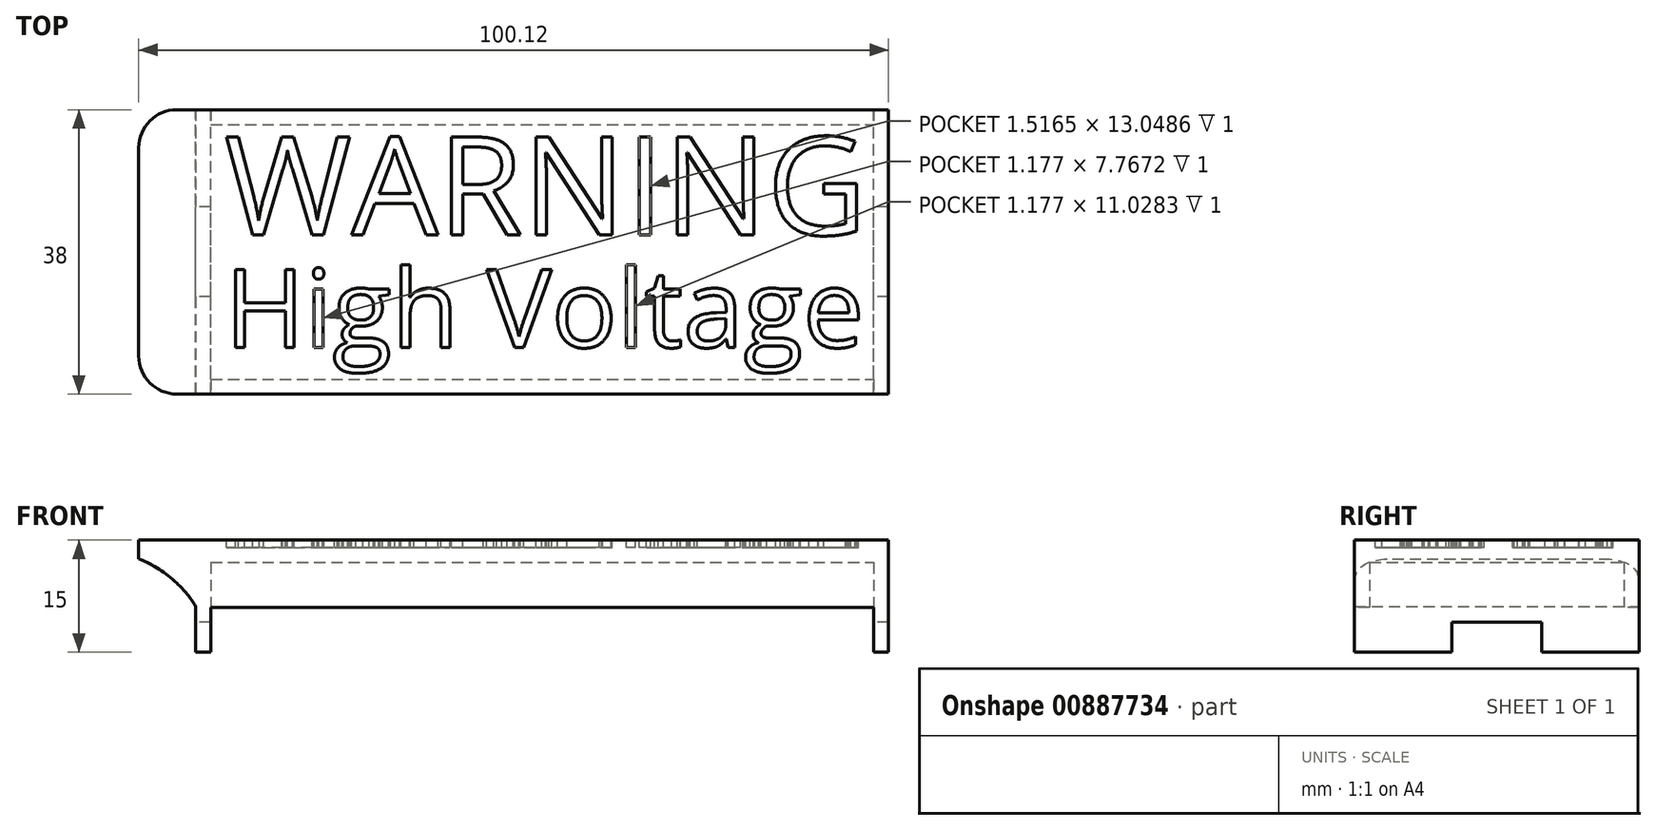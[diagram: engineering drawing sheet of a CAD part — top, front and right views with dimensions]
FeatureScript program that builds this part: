
annotation { "Feature Type Name" : "Feature", "Feature Type Description" : "" }
export const myFeature = defineFeature(function(context is Context, id is Id, definition is map)
    precondition{}
    {
        {
            var Q0;
            Q0=qCreatedBy(makeId("Top.planeOp"),FACE);
            var sketch = newSketch(context, id + "F0", { "sketchPlane" : qUnion([Q0])});
            skLineSegment(sketch, "E0.bottom", {"start": v(-44.25, -17) * mm, "end": v(44.25, -17) * mm});
            skLineSegment(sketch, "E0.top", {"start": v(-44.25, 17) * mm, "end": v(44.25, 17) * mm});
            skLineSegment(sketch, "E0.left", {"start": v(-44.25, -17) * mm, "end": v(-44.25, 17) * mm});
            skLineSegment(sketch, "E0.right", {"start": v(44.25, -17) * mm, "end": v(44.25, 17) * mm});
            skLineSegment(sketch, "E1.bottom", {"start": v(46.25, 19) * mm, "end": v(-46.25, 19) * mm});
            skLineSegment(sketch, "E1.top", {"start": v(46.25, -19) * mm, "end": v(-46.25, -19) * mm});
            skLineSegment(sketch, "E1.left", {"start": v(46.25, 19) * mm, "end": v(46.25, -19) * mm});
            skLineSegment(sketch, "E1.right", {"start": v(-46.25, 19) * mm, "end": v(-46.25, -19) * mm});
            skPoint(sketch, "E1.middle", {"position": v(0, 0) * mm});
            skSolve(sketch);
        }
        {
            var Q0;
            Q0=makeQuery(id+"F0.imprint","IMPRINT",FACE,{"disambiguationData":[TD([[makeQuery(id+"F0.imprint","IMPRINT",EDGE,{"derivedFrom":sQuery(id+"F0.wireOp",EDGE,"E0.bottom")}),-1.0]])]});
            extrude(context, id + "F1", {"entities" : qUnion([Q0]), "depth" : 12 * mm, "offsetDistance" : 25.4 * mm});
        }
        {
            var Q0;
            Q0=makeQuery(id+"F1.opExtrude","SWEPT_FACE",FACE,{"disambiguationData":[OSD([sQuery(id+"F0.wireOp",EDGE,"E1.top")])]});
            var sketch = newSketch(context, id + "F2", { "sketchPlane" : qUnion([Q0])});
            skLineSegment(sketch, "E2.bottom", {"start": v(44.25, 6) * mm, "end": v(-44.25, 6) * mm});
            skLineSegment(sketch, "E2.top", {"start": v(44.25, -6) * mm, "end": v(-44.25, -6) * mm});
            skLineSegment(sketch, "E2.left", {"start": v(44.25, 6) * mm, "end": v(44.25, -6) * mm});
            skLineSegment(sketch, "E2.right", {"start": v(-44.25, 6) * mm, "end": v(-44.25, -6) * mm});
            skPoint(sketch, "E2.middle", {"position": v(0, 0) * mm});
            skSolve(sketch);
        }
        {
            var Q0;
            Q0 = qSketchRegion(id + "F2", true);
            extrude(context, id + "F3", {"entities" : qUnion([Q0]), "operationType" : NewBodyOperationType.REMOVE, "oppositeDirection" : true, "depth" : 48.26 * mm, "offsetDistance" : 25.4 * mm});
        }
        {
            var Q0;
            Q0=makeQuery(id+"F1.opExtrude","CAP_FACE",FACE,{"disambiguationData":[OSD([sQuery(id+"F0.wireOp",EDGE,"E0.bottom"),sQuery(id+"F0.wireOp",EDGE,"E0.top"),sQuery(id+"F0.wireOp",EDGE,"E0.left"),sQuery(id+"F0.wireOp",EDGE,"E0.right"),sQuery(id+"F0.wireOp",EDGE,"E1.bottom"),sQuery(id+"F0.wireOp",EDGE,"E1.top"),sQuery(id+"F0.wireOp",EDGE,"E1.left"),sQuery(id+"F0.wireOp",EDGE,"E1.right")])],"isStart":false});
            var sketch = newSketch(context, id + "F4", { "sketchPlane" : qUnion([Q0])});
            skLineSegment(sketch, "E3.bottom", {"start": v(46.25, 19) * mm, "end": v(-46.25, 19) * mm});
            skLineSegment(sketch, "E3.top", {"start": v(46.25, -19) * mm, "end": v(-46.25, -19) * mm});
            skLineSegment(sketch, "E3.left", {"start": v(46.25, 19) * mm, "end": v(46.25, -19) * mm});
            skLineSegment(sketch, "E3.right", {"start": v(-46.25, 19) * mm, "end": v(-46.25, -19) * mm});
            skPoint(sketch, "E3.middle", {"position": v(0, 0) * mm});
            skSolve(sketch);
        }
        {
            var Q0;
            Q0 = qSketchRegion(id + "F4", true);
            extrude(context, id + "F5", {"entities" : qUnion([Q0]), "operationType" : NewBodyOperationType.ADD, "depth" : 3 * mm, "offsetDistance" : 25.4 * mm});
        }
        {
            var Q0;
            Q0=makeQuery(id+"F5.opExtrude","CAP_FACE",FACE,{"disambiguationData":[OSD([sQuery(id+"F4.wireOp",EDGE,"E3.bottom"),sQuery(id+"F4.wireOp",EDGE,"E3.top"),sQuery(id+"F4.wireOp",EDGE,"E3.left"),sQuery(id+"F4.wireOp",EDGE,"E3.right")])],"isStart":false});
            var sketch = newSketch(context, id + "F6", { "sketchPlane" : qUnion([Q0])});
            skText(sketch, "E4", { "text": "WARNING", "fontName": "OpenSans-Regular.ttf"});
            skText(sketch, "E5", { "text": "High Voltage", "fontName": "OpenSans-Regular.ttf"});
            const initialGuessF6  = {"E4": [-0.0424, 0.00229, 1, 0, 0.01316], "E5": [-0.0424, -0.01274, 1, 0, 0.01045]};
            skSetInitialGuess(sketch, initialGuessF6);
            skSolve(sketch);
        }
        {
            var Q0;
            Q0 = qSketchRegion(id + "F6", true);
            extrude(context, id + "F7", {"entities" : qUnion([Q0]), "operationType" : NewBodyOperationType.REMOVE, "oppositeDirection" : true, "depth" : 1 * mm, "offsetDistance" : 25.4 * mm});
        }
        {
            var Q0;
            Q0=qCreatedBy(makeId("Front.planeOp"),FACE);
            var sketch = newSketch(context, id + "F8", { "sketchPlane" : qUnion([Q0])});
            skLineSegment(sketch, "E6.bottom", {"start": v(-46.25, 15) * mm, "end": v(-53.87, 15) * mm});
            skLineSegment(sketch, "E6.top", {"start": v(-46.25, 6.14) * mm, "end": v(-53.87, 6.14) * mm});
            skLineSegment(sketch, "E6.left", {"start": v(-46.25, 15) * mm, "end": v(-46.25, 6.14) * mm});
            skLineSegment(sketch, "E6.right", {"start": v(-53.87, 15) * mm, "end": v(-53.87, 6.14) * mm});
            skPoint(sketch, "E6.middle", {"position": v(-50.06, 10.57) * mm});
            skArc(sketch, "E7", {"start": v(-46.25, 6.14) * mm, "mid": v(-49.56, 9.92) * mm, "end": v(-53.87, 12.5) * mm});
            skArc(sketch, "E8.MirrorCS", {"start": v(46.25, 6.14) * mm, "mid": v(49.56, 9.92) * mm, "end": v(53.87, 12.5) * mm});
            skLineSegment(sketch, "E9.MirrorCS", {"start": v(46.25, 15) * mm, "end": v(46.25, 6.14) * mm});
            skLineSegment(sketch, "E10.MirrorCS", {"start": v(46.25, 15) * mm, "end": v(53.87, 15) * mm});
            skLineSegment(sketch, "E11.MirrorCS", {"start": v(53.87, 15) * mm, "end": v(53.87, 6.14) * mm});
            skSolve(sketch);
        }
        {
            var Q0;
            {var subQ0=sQuery(id+"F8.wireOp",EDGE,"E6.bottom");Q0=makeQuery(id+"F8.imprint","IMPRINT",FACE,{"disambiguationData":[TD([[makeQuery(id+"F8.imprint","IMPRINT",EDGE,{"derivedFrom":subQ0}),1.0]])]});}
            var Q1;
            {var subQ0=sQuery(id+"F8.wireOp",EDGE,"E8.MirrorCS");Q1=makeQuery(id+"F8.imprint","IMPRINT",FACE,{"disambiguationData":[TD([[makeQuery(id+"F8.imprint","IMPRINT",EDGE,{"derivedFrom":subQ0}),1.0]])]});}
            var Q2;
            Q2=makeQuery(id+"F5.boolean.opBoolean","MERGE",FACE,{"derivedFrom":[makeQuery(id+"F1.opExtrude","SWEPT_FACE",FACE,{"disambiguationData":[OSD([sQuery(id+"F0.wireOp",EDGE,"E1.top")])]}),makeQuery(id+"F5.opExtrude","SWEPT_FACE",FACE,{"disambiguationData":[OSD([sQuery(id+"F4.wireOp",EDGE,"E3.top")])]})]});
            var Q3;
            Q3=makeQuery(id+"F5.boolean.opBoolean","MERGE",FACE,{"derivedFrom":[makeQuery(id+"F1.opExtrude","SWEPT_FACE",FACE,{"disambiguationData":[OSD([sQuery(id+"F0.wireOp",EDGE,"E1.bottom")])]}),makeQuery(id+"F5.opExtrude","SWEPT_FACE",FACE,{"disambiguationData":[OSD([sQuery(id+"F4.wireOp",EDGE,"E3.bottom")])]})]});
            extrude(context, id + "F9", {"entities" : qUnion([Q0, Q1]), "operationType" : NewBodyOperationType.ADD, "endBound" : BoundingType.UP_TO_SURFACE, "depth" : 25.4 * mm, "endBoundEntityFace" : qUnion([Q2]), "offsetDistance" : 25.4 * mm, "hasSecondDirection" : true, "secondDirectionBound" : SecondDirectionBoundingType.UP_TO_SURFACE, "secondDirectionOppositeDirection" : true, "secondDirectionDepth" : 25.4 * mm, "secondDirectionBoundEntityFace" : qUnion([Q3])});
        }
        {
            var Q0;
            Q0=makeQuery(id+"F9.opExtrude","CAP_EDGE",EDGE,{"disambiguationData":[OSD([sQuery(id+"F8.wireOp",EDGE,"E6.right")])],"isStart":false});
            var Q1;
            Q1=makeQuery(id+"F9.opExtrude","CAP_EDGE",EDGE,{"disambiguationData":[OSD([sQuery(id+"F8.wireOp",EDGE,"E6.right")])],"isStart":true});
            var Q2;
            Q2=makeQuery(id+"F9.opExtrude","CAP_EDGE",EDGE,{"disambiguationData":[OSD([sQuery(id+"F8.wireOp",EDGE,"E11.MirrorCS")])],"isStart":false});
            var Q3;
            Q3=makeQuery(id+"F9.opExtrude","CAP_EDGE",EDGE,{"disambiguationData":[OSD([sQuery(id+"F8.wireOp",EDGE,"E11.MirrorCS")])],"isStart":true});
            fillet(context, id + "F10", {"entities" : qUnion([Q0, Q1, Q2, Q3]), "radius" : 5.08 * mm, "tangentPropagation" : true, "allowEdgeOverflow" : false});
        }
        {
            var Q0;
            Q0=makeQuery(id+"F5.boolean.opBoolean","MERGE",FACE,{"derivedFrom":[makeQuery(id+"F1.opExtrude","SWEPT_FACE",FACE,{"disambiguationData":[OSD([sQuery(id+"F0.wireOp",EDGE,"E1.right")])]}),makeQuery(id+"F5.opExtrude","SWEPT_FACE",FACE,{"disambiguationData":[OSD([sQuery(id+"F4.wireOp",EDGE,"E3.right")])]})]});
            var sketch = newSketch(context, id + "F11", { "sketchPlane" : qUnion([Q0])});
            skLineSegment(sketch, "E12.bottom", {"start": v(6, 4) * mm, "end": v(-6, 4) * mm});
            skLineSegment(sketch, "E12.top", {"start": v(6, -4) * mm, "end": v(-6, -4) * mm});
            skLineSegment(sketch, "E12.left", {"start": v(6, 4) * mm, "end": v(6, -4) * mm});
            skLineSegment(sketch, "E12.right", {"start": v(-6, 4) * mm, "end": v(-6, -4) * mm});
            skPoint(sketch, "E12.middle", {"position": v(0, 0) * mm});
            skSolve(sketch);
        }
        {
            var Q0;
            {var subQ0=sQuery(id+"F11.wireOp",EDGE,"E12.bottom");Q0=makeQuery(id+"F11.imprint","IMPRINT",FACE,{"disambiguationData":[TD([[makeQuery(id+"F11.imprint","IMPRINT",EDGE,{"derivedFrom":subQ0}),1.0]])]});}
            extrude(context, id + "F12", {"entities" : qUnion([Q0]), "operationType" : NewBodyOperationType.REMOVE, "endBound" : BoundingType.THROUGH_ALL, "oppositeDirection" : true, "depth" : 25.4 * mm, "offsetDistance" : 25.4 * mm});
        }
    });
